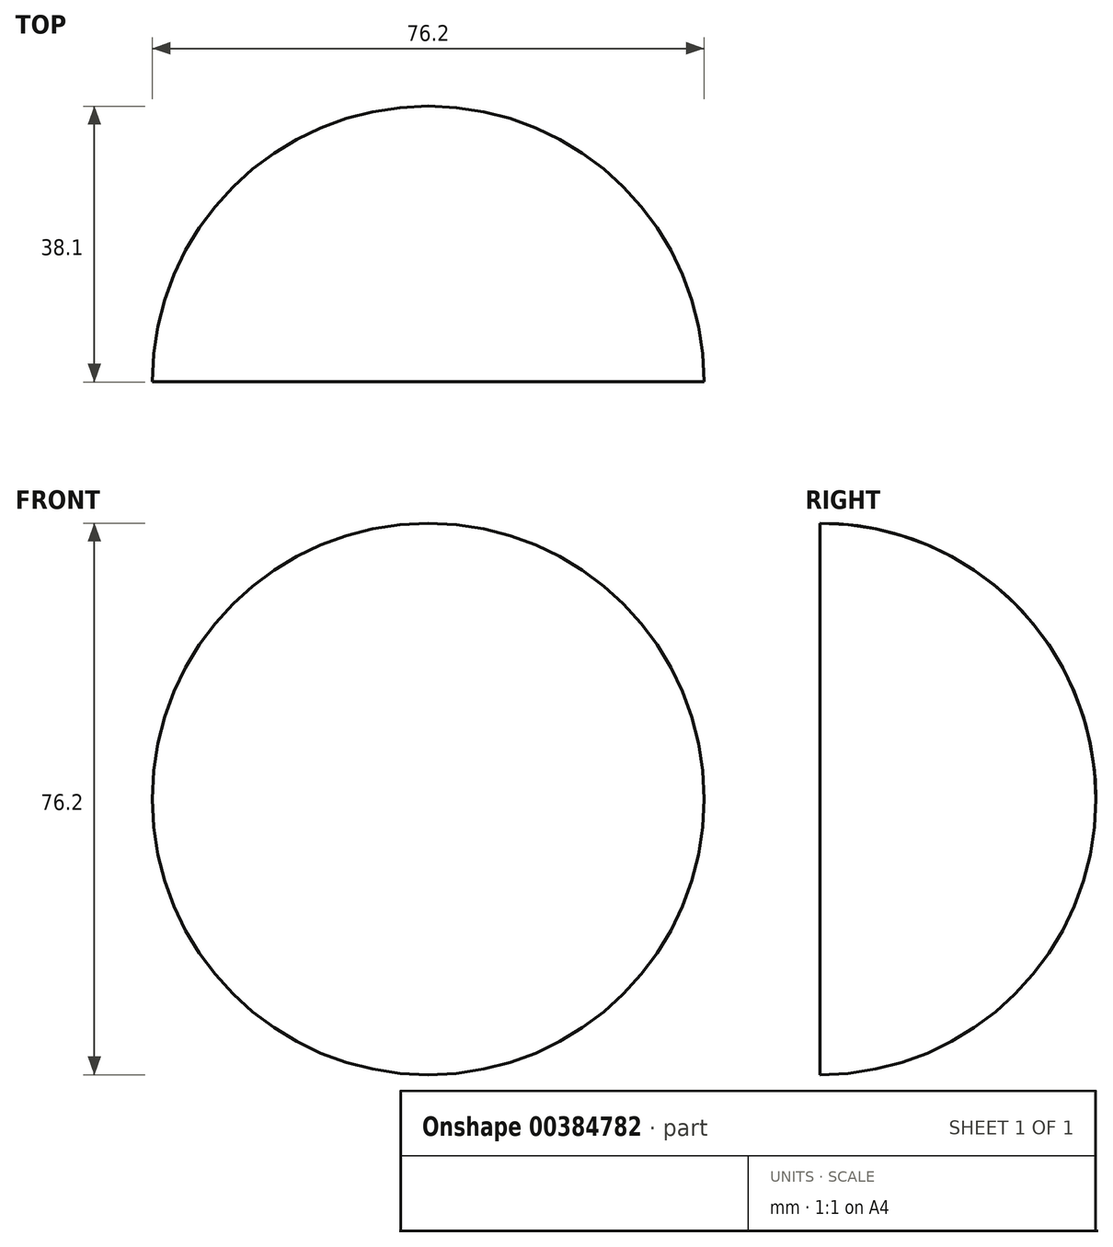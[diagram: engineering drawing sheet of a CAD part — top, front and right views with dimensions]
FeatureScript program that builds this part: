
annotation { "Feature Type Name" : "Feature", "Feature Type Description" : "" }
export const myFeature = defineFeature(function(context is Context, id is Id, definition is map)
    precondition{}
    {
        {
            var Q0;
            Q0=qCreatedBy(makeId("Right.planeOp"),FACE);
            var sketch = newSketch(context, id + "F0", { "sketchPlane" : qUnion([Q0])});
            skLineSegment(sketch, "E0", {"start": v(-62.4, 25.23) * mm, "end": v(13.8, 25.23) * mm});
            skLineSegment(sketch, "E1", {"start": v(-62.4, 25.23) * mm, "end": v(-24.3, 25.23) * mm});
            skLineSegment(sketch, "E2", {"start": v(-24.3, 25.23) * mm, "end": v(-24.3, 63.33) * mm});
            skArc(sketch, "E3", {"start": v(13.8, 25.23) * mm, "mid": v(-24.3, 63.33) * mm, "end": v(-62.4, 25.23) * mm});
            skLineSegment(sketch, "E4", {"start": v(13.8, 25.23) * mm, "end": v(13.78, 25.23) * mm});
            skLineSegment(sketch, "E5", {"start": v(13.78, 25.23) * mm, "end": v(-24.3, 25.23) * mm});
            skLineSegment(sketch, "E6", {"start": v(-24.3, 25.23) * mm, "end": v(-24.3, 63.3) * mm});
            skLineSegment(sketch, "E7", {"start": v(-24.3, 25.23) * mm, "end": v(-62.37, 25.23) * mm});
            skArc(sketch, "E8", {"start": v(13.8, 25.23) * mm, "mid": v(-24.28, 63.33) * mm, "end": v(-62.37, 25.23) * mm});
            skSolve(sketch);
        }
        {
            var Q0;
            {var subQ3=sQuery(id+"F0.wireOp",EDGE,"E2");Q0=makeQuery(id+"F0.imprint","IMPRINT",FACE,{"disambiguationData":[TD([[makeQuery(id+"F0.imprint","IMPRINT",EDGE,{"derivedFrom":subQ3}),-1.0]])]});}
            var Q1;
            Q1=sQuery(id+"F0.wireOp",EDGE,"E7");
            revolve(context, id + "F1", {"entities" : qUnion([Q0]), "axis" : qUnion([Q1]), "revolveType" : RevolveType.FULL});
        }
    });
